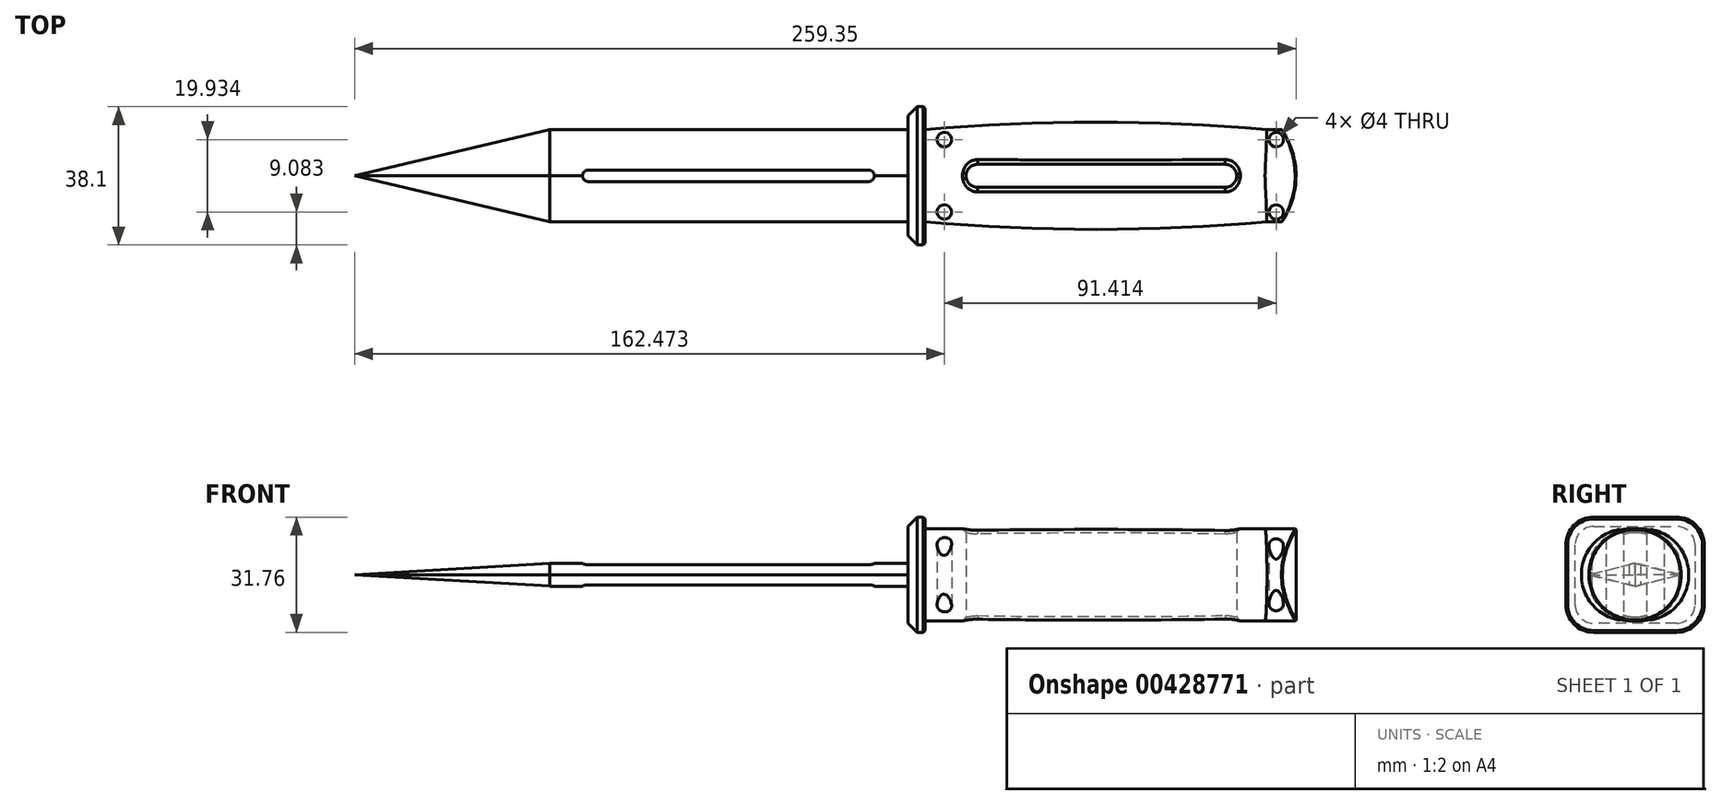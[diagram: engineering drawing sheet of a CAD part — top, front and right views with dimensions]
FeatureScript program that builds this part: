
annotation { "Feature Type Name" : "Feature", "Feature Type Description" : "" }
export const myFeature = defineFeature(function(context is Context, id is Id, definition is map)
    precondition{}
    {
        {
            var Q0;
            Q0=qCreatedBy(makeId("Top.planeOp"),FACE);
            var sketch = newSketch(context, id + "F0", { "sketchPlane" : qUnion([Q0])});
            skPoint(sketch, "E0.middle", {"position": v(0, 0) * mm});
            skLineSegment(sketch, "E1", {"start": v(-130.18, 0) * mm, "end": v(-76.43, 12.7) * mm});
            skLineSegment(sketch, "E2.MirrorCS", {"start": v(-130.18, 0) * mm, "end": v(-76.43, -12.7) * mm});
            skLineSegment(sketch, "E3", {"start": v(-76.43, 12.7) * mm, "end": v(22.22, 12.7) * mm});
            skLineSegment(sketch, "E4.MirrorCS", {"start": v(-76.43, -12.7) * mm, "end": v(22.22, -12.7) * mm});
            skLineSegment(sketch, "E5", {"start": v(-76.43, 12.7) * mm, "end": v(-76.43, 0) * mm});
            skLineSegment(sketch, "E6", {"start": v(-76.43, 0) * mm, "end": v(-76.43, -12.7) * mm});
            skLineSegment(sketch, "E7", {"start": v(-130.18, 0) * mm, "end": v(-76.43, 0) * mm});
            skLineSegment(sketch, "E8", {"start": v(22.22, 12.7) * mm, "end": v(22.22, -12.7) * mm});
            skLineSegment(sketch, "E9", {"start": v(22.22, 12.7) * mm, "end": v(22.22, 19.05) * mm});
            skLineSegment(sketch, "E10", {"start": v(22.22, 19.05) * mm, "end": v(27, 19.05) * mm});
            skLineSegment(sketch, "E11", {"start": v(27, 19.05) * mm, "end": v(27, 12.7) * mm});
            skLineSegment(sketch, "E12.MirrorCS", {"start": v(22.22, -12.7) * mm, "end": v(22.22, -19.05) * mm});
            skLineSegment(sketch, "E13.MirrorCS", {"start": v(22.22, -19.05) * mm, "end": v(27, -19.05) * mm});
            skLineSegment(sketch, "E14.MirrorCS", {"start": v(27, -19.05) * mm, "end": v(27, -12.7) * mm});
            skLineSegment(sketch, "E15", {"start": v(-65.78, 0) * mm, "end": v(11.43, 0) * mm});
            skArc(sketch, "E16.0.startCap", {"start": v(-65.78, -1.59) * mm, "mid": v(-67.36, 0) * mm, "end": v(-65.78, 1.59) * mm});
            skArc(sketch, "E16.0.endCap", {"start": v(11.43, 1.59) * mm, "mid": v(13.02, 0) * mm, "end": v(11.43, -1.59) * mm});
            skLineSegment(sketch, "E16.0.left", {"start": v(-65.78, 1.59) * mm, "end": v(11.43, 1.59) * mm});
            skLineSegment(sketch, "E16.0.right", {"start": v(-65.78, -1.59) * mm, "end": v(11.43, -1.59) * mm});
            skArc(sketch, "E17", {"start": v(121.17, 12.7) * mm, "mid": v(74.08, 14.77) * mm, "end": v(27, 12.7) * mm});
            skArc(sketch, "E18.MirrorCS", {"start": v(121.17, -12.7) * mm, "mid": v(74.08, -14.77) * mm, "end": v(27, -12.7) * mm});
            skArc(sketch, "E19", {"start": v(125.3, -12.7) * mm, "mid": v(129.17, 0) * mm, "end": v(125.3, 12.7) * mm});
            skFitSpline(sketch, "E20", {"points": [v(121.17, -12.7) * mm, v(125.3, -12.7) * mm], "startDerivative": vector(4.13, 0) * mm, "endDerivative": vector(4.13, 0) * mm});
            skFitSpline(sketch, "E21.MirrorCS", {"points": [v(121.17, 12.7) * mm, v(125.3, 12.7) * mm], "startDerivative": vector(4.13, 0) * mm, "endDerivative": vector(4.13, 0) * mm});
            skCircle(sketch, "E22", {"center": v(123.7, 9.97) * mm, "radius": 2 * mm});
            skCircle(sketch, "E23.MirrorC", {"center": v(123.7, -9.97) * mm, "radius": 2 * mm});
            skCircle(sketch, "E24", {"center": v(32.3, 9.97) * mm, "radius": 2 * mm});
            skCircle(sketch, "E25.MirrorC", {"center": v(32.3, -9.97) * mm, "radius": 2 * mm});
            skLineSegment(sketch, "E26", {"start": v(41.46, 0) * mm, "end": v(109.63, 0) * mm});
            skArc(sketch, "E27.0.startCap", {"start": v(41.46, -3.18) * mm, "mid": v(38.28, 0) * mm, "end": v(41.46, 3.18) * mm});
            skArc(sketch, "E27.0.endCap", {"start": v(109.63, 3.18) * mm, "mid": v(112.8, 0) * mm, "end": v(109.63, -3.18) * mm});
            skLineSegment(sketch, "E27.0.left", {"start": v(41.46, 3.18) * mm, "end": v(109.63, 3.18) * mm});
            skLineSegment(sketch, "E27.0.right", {"start": v(41.46, -3.18) * mm, "end": v(109.63, -3.18) * mm});
            skLineSegment(sketch, "E28", {"start": v(27, 12.7) * mm, "end": v(27, -12.7) * mm});
            skSolve(sketch);
        }
        {
            var Q0;
            Q0=makeQuery(id+"F0.imprint","IMPRINT",FACE,{"disambiguationData":[TD([[makeQuery(id+"F0.imprint","IMPRINT",EDGE,{"derivedFrom":sQuery(id+"F0.wireOp",EDGE,"E17")}),1.0]])]});
            extrude(context, id + "F1", {"entities" : qUnion([Q0]), "depth" : 25.4 * mm});
        }
        {
            var Q0;
            Q0=makeQuery(id+"F1.opExtrude","CAP_EDGE",EDGE,{"disambiguationData":[OSD([sQuery(id+"F0.wireOp",EDGE,"E17")])],"isStart":false});
            var Q1;
            Q1=makeQuery(id+"F1.opExtrude","CAP_EDGE",EDGE,{"disambiguationData":[OSD([sQuery(id+"F0.wireOp",EDGE,"E21.MirrorCS")])],"isStart":false});
            var Q2;
            Q2=makeQuery(id+"F1.opExtrude","CAP_EDGE",EDGE,{"disambiguationData":[OSD([sQuery(id+"F0.wireOp",EDGE,"E20")])],"isStart":false});
            var Q3;
            Q3=makeQuery(id+"F1.opExtrude","CAP_EDGE",EDGE,{"disambiguationData":[OSD([sQuery(id+"F0.wireOp",EDGE,"E18.MirrorCS")])],"isStart":false});
            var Q4;
            Q4=makeQuery(id+"F1.opExtrude","CAP_EDGE",EDGE,{"disambiguationData":[OSD([sQuery(id+"F0.wireOp",EDGE,"E18.MirrorCS")])],"isStart":true});
            var Q5;
            Q5=makeQuery(id+"F1.opExtrude","CAP_EDGE",EDGE,{"disambiguationData":[OSD([sQuery(id+"F0.wireOp",EDGE,"E20")])],"isStart":true});
            var Q6;
            Q6=makeQuery(id+"F1.opExtrude","CAP_EDGE",EDGE,{"disambiguationData":[OSD([sQuery(id+"F0.wireOp",EDGE,"E17")])],"isStart":true});
            var Q7;
            Q7=makeQuery(id+"F1.opExtrude","CAP_EDGE",EDGE,{"disambiguationData":[OSD([sQuery(id+"F0.wireOp",EDGE,"E21.MirrorCS")])],"isStart":true});
            fillet(context, id + "F2", {"entities" : qUnion([Q0, Q1, Q2, Q3, Q4, Q5, Q6, Q7]), "radius" : 12.67 * mm, "tangentPropagation" : true, "allowEdgeOverflow" : false});
        }
        {
            var Q0;
            Q0=makeQuery(id+"F0.imprint","IMPRINT",FACE,{"disambiguationData":[TD([[makeQuery(id+"F0.imprint","IMPRINT",EDGE,{"derivedFrom":sQuery(id+"F0.wireOp",EDGE,"E8")}),1.0]])]});
            extrude(context, id + "F3", {"entities" : qUnion([Q0]), "depth" : 28.57 * mm, "hasSecondDirection" : true, "secondDirectionOppositeDirection" : true, "secondDirectionDepth" : 3.17 * mm});
        }
        {
            var Q0;
            Q0=makeQuery(id+"F3.opExtrude","CAP_EDGE",EDGE,{"disambiguationData":[OSD([sQuery(id+"F0.wireOp",EDGE,"E10")])],"isStart":false});
            var Q1;
            Q1=makeQuery(id+"F3.opExtrude","CAP_EDGE",EDGE,{"disambiguationData":[OSD([sQuery(id+"F0.wireOp",EDGE,"E10")])],"isStart":true});
            var Q2;
            Q2=makeQuery(id+"F3.opExtrude","CAP_EDGE",EDGE,{"disambiguationData":[OSD([sQuery(id+"F0.wireOp",EDGE,"E13.MirrorCS")])],"isStart":true});
            var Q3;
            Q3=makeQuery(id+"F3.opExtrude","CAP_EDGE",EDGE,{"disambiguationData":[OSD([sQuery(id+"F0.wireOp",EDGE,"E13.MirrorCS")])],"isStart":false});
            fillet(context, id + "F4", {"entities" : qUnion([Q0, Q1, Q2, Q3]), "radius" : 7.62 * mm, "tangentPropagation" : true, "allowEdgeOverflow" : false});
        }
        {
            var Q0;
            Q0=makeQuery(id+"F3.opExtrude","CAP_EDGE",EDGE,{"disambiguationData":[OSD([sQuery(id+"F0.wireOp",EDGE,"E8"),sQuery(id+"F0.wireOp",EDGE,"E9"),sQuery(id+"F0.wireOp",EDGE,"E12.MirrorCS")])],"isStart":false});
            chamfer(context, id + "F5", {"entities" : qUnion([Q0]), "width" : 2.54 * mm, "tangentPropagation" : true});
        }
        {
            var Q0;
            Q0=makeQuery(id+"F3.opExtrude","CAP_EDGE",EDGE,{"disambiguationData":[OSD([sQuery(id+"F0.wireOp",EDGE,"E11"),sQuery(id+"F0.wireOp",EDGE,"E14.MirrorCS"),sQuery(id+"F0.wireOp",EDGE,"E28")])],"isStart":false});
            chamfer(context, id + "F6", {"entities" : qUnion([Q0]), "width" : 0.5 * mm, "tangentPropagation" : true});
        }
        {
            var Q0;
            Q0=makeQuery(id+"F2.opFillet","BLEND_EDGE",EDGE,{"blendedFrom":[makeQuery(id+"F1.opExtrude","CAP_EDGE",EDGE,{"disambiguationData":[OSD([sQuery(id+"F0.wireOp",EDGE,"E21.MirrorCS")])],"isStart":false}),makeQuery(id+"F1.opExtrude","SWEPT_FACE",FACE,{"disambiguationData":[OSD([sQuery(id+"F0.wireOp",EDGE,"E19")])]})],"blendedInto":[makeQuery(id+"F1.opExtrude","SWEPT_FACE",FACE,{"disambiguationData":[OSD([sQuery(id+"F0.wireOp",EDGE,"E19")])]})]});
            var Q1;
            Q1=makeQuery(id+"F2.opFillet","BLEND_EDGE",EDGE,{"blendedFrom":[makeQuery(id+"F1.opExtrude","CAP_EDGE",EDGE,{"disambiguationData":[OSD([sQuery(id+"F0.wireOp",EDGE,"E21.MirrorCS")])],"isStart":true}),makeQuery(id+"F1.opExtrude","SWEPT_FACE",FACE,{"disambiguationData":[OSD([sQuery(id+"F0.wireOp",EDGE,"E19")])]})],"blendedInto":[makeQuery(id+"F1.opExtrude","SWEPT_FACE",FACE,{"disambiguationData":[OSD([sQuery(id+"F0.wireOp",EDGE,"E19")])]})]});
            var Q2;
            Q2=makeQuery(id+"F2.opFillet","BLEND_EDGE",EDGE,{"blendedFrom":[makeQuery(id+"F1.opExtrude","CAP_EDGE",EDGE,{"disambiguationData":[OSD([sQuery(id+"F0.wireOp",EDGE,"E20")])],"isStart":true}),makeQuery(id+"F1.opExtrude","SWEPT_FACE",FACE,{"disambiguationData":[OSD([sQuery(id+"F0.wireOp",EDGE,"E19")])]})],"blendedInto":[makeQuery(id+"F1.opExtrude","SWEPT_FACE",FACE,{"disambiguationData":[OSD([sQuery(id+"F0.wireOp",EDGE,"E19")])]})]});
            var Q3;
            Q3=makeQuery(id+"F2.opFillet","BLEND_EDGE",EDGE,{"blendedFrom":[makeQuery(id+"F1.opExtrude","CAP_EDGE",EDGE,{"disambiguationData":[OSD([sQuery(id+"F0.wireOp",EDGE,"E20")])],"isStart":false}),makeQuery(id+"F1.opExtrude","SWEPT_FACE",FACE,{"disambiguationData":[OSD([sQuery(id+"F0.wireOp",EDGE,"E19")])]})],"blendedInto":[makeQuery(id+"F1.opExtrude","SWEPT_FACE",FACE,{"disambiguationData":[OSD([sQuery(id+"F0.wireOp",EDGE,"E19")])]})]});
            chamfer(context, id + "F7", {"entities" : qUnion([Q0, Q1, Q2, Q3]), "width" : 0.25 * mm, "tangentPropagation" : true});
        }
        {
            var Q0;
            Q0=makeQuery(id+"F2.opFillet","BLEND_EDGE",EDGE,{"blendedFrom":[makeQuery(id+"F1.opExtrude","CAP_EDGE",EDGE,{"disambiguationData":[OSD([sQuery(id+"F0.wireOp",EDGE,"E17")])],"isStart":false}),makeQuery(id+"F1.opExtrude","SWEPT_FACE",FACE,{"disambiguationData":[OSD([sQuery(id+"F0.wireOp",EDGE,"E27.0.left")])]})],"blendedInto":[makeQuery(id+"F1.opExtrude","SWEPT_FACE",FACE,{"disambiguationData":[OSD([sQuery(id+"F0.wireOp",EDGE,"E27.0.left")])]})]});
            var Q1;
            Q1=makeQuery(id+"F2.opFillet","BLEND_EDGE",EDGE,{"blendedFrom":[makeQuery(id+"F1.opExtrude","CAP_EDGE",EDGE,{"disambiguationData":[OSD([sQuery(id+"F0.wireOp",EDGE,"E17")])],"isStart":false}),makeQuery(id+"F1.opExtrude","SWEPT_FACE",FACE,{"disambiguationData":[OSD([sQuery(id+"F0.wireOp",EDGE,"E27.0.startCap")])]})],"blendedInto":[makeQuery(id+"F1.opExtrude","SWEPT_FACE",FACE,{"disambiguationData":[OSD([sQuery(id+"F0.wireOp",EDGE,"E27.0.startCap")])]})]});
            var Q2;
            Q2=makeQuery(id+"F1.opExtrude","CAP_EDGE",EDGE,{"disambiguationData":[OSD([sQuery(id+"F0.wireOp",EDGE,"E27.0.startCap")])],"isStart":false});
            var Q3;
            Q3=makeQuery(id+"F2.opFillet","BLEND_EDGE",EDGE,{"blendedFrom":[makeQuery(id+"F1.opExtrude","CAP_EDGE",EDGE,{"disambiguationData":[OSD([sQuery(id+"F0.wireOp",EDGE,"E18.MirrorCS")])],"isStart":false}),makeQuery(id+"F1.opExtrude","SWEPT_FACE",FACE,{"disambiguationData":[OSD([sQuery(id+"F0.wireOp",EDGE,"E27.0.startCap")])]})],"blendedInto":[makeQuery(id+"F1.opExtrude","SWEPT_FACE",FACE,{"disambiguationData":[OSD([sQuery(id+"F0.wireOp",EDGE,"E27.0.startCap")])]})]});
            var Q4;
            Q4=makeQuery(id+"F2.opFillet","BLEND_EDGE",EDGE,{"blendedFrom":[makeQuery(id+"F1.opExtrude","CAP_EDGE",EDGE,{"disambiguationData":[OSD([sQuery(id+"F0.wireOp",EDGE,"E18.MirrorCS")])],"isStart":false}),makeQuery(id+"F1.opExtrude","SWEPT_FACE",FACE,{"disambiguationData":[OSD([sQuery(id+"F0.wireOp",EDGE,"E27.0.right")])]})],"blendedInto":[makeQuery(id+"F1.opExtrude","SWEPT_FACE",FACE,{"disambiguationData":[OSD([sQuery(id+"F0.wireOp",EDGE,"E27.0.right")])]})]});
            var Q5;
            Q5=makeQuery(id+"F2.opFillet","BLEND_EDGE",EDGE,{"blendedFrom":[makeQuery(id+"F1.opExtrude","CAP_EDGE",EDGE,{"disambiguationData":[OSD([sQuery(id+"F0.wireOp",EDGE,"E18.MirrorCS")])],"isStart":false}),makeQuery(id+"F1.opExtrude","SWEPT_FACE",FACE,{"disambiguationData":[OSD([sQuery(id+"F0.wireOp",EDGE,"E27.0.endCap")])]})],"blendedInto":[makeQuery(id+"F1.opExtrude","SWEPT_FACE",FACE,{"disambiguationData":[OSD([sQuery(id+"F0.wireOp",EDGE,"E27.0.endCap")])]})]});
            var Q6;
            Q6=makeQuery(id+"F1.opExtrude","CAP_EDGE",EDGE,{"disambiguationData":[OSD([sQuery(id+"F0.wireOp",EDGE,"E27.0.endCap")])],"isStart":false});
            var Q7;
            Q7=makeQuery(id+"F2.opFillet","BLEND_EDGE",EDGE,{"blendedFrom":[makeQuery(id+"F1.opExtrude","CAP_EDGE",EDGE,{"disambiguationData":[OSD([sQuery(id+"F0.wireOp",EDGE,"E17")])],"isStart":false}),makeQuery(id+"F1.opExtrude","SWEPT_FACE",FACE,{"disambiguationData":[OSD([sQuery(id+"F0.wireOp",EDGE,"E27.0.endCap")])]})],"blendedInto":[makeQuery(id+"F1.opExtrude","SWEPT_FACE",FACE,{"disambiguationData":[OSD([sQuery(id+"F0.wireOp",EDGE,"E27.0.endCap")])]})]});
            var Q8;
            Q8=makeQuery(id+"F2.opFillet","BLEND_EDGE",EDGE,{"blendedFrom":[makeQuery(id+"F1.opExtrude","CAP_EDGE",EDGE,{"disambiguationData":[OSD([sQuery(id+"F0.wireOp",EDGE,"E17")])],"isStart":true}),makeQuery(id+"F1.opExtrude","SWEPT_FACE",FACE,{"disambiguationData":[OSD([sQuery(id+"F0.wireOp",EDGE,"E27.0.left")])]})],"blendedInto":[makeQuery(id+"F1.opExtrude","SWEPT_FACE",FACE,{"disambiguationData":[OSD([sQuery(id+"F0.wireOp",EDGE,"E27.0.left")])]})]});
            var Q9;
            Q9=makeQuery(id+"F2.opFillet","BLEND_EDGE",EDGE,{"blendedFrom":[makeQuery(id+"F1.opExtrude","CAP_EDGE",EDGE,{"disambiguationData":[OSD([sQuery(id+"F0.wireOp",EDGE,"E18.MirrorCS")])],"isStart":true}),makeQuery(id+"F1.opExtrude","SWEPT_FACE",FACE,{"disambiguationData":[OSD([sQuery(id+"F0.wireOp",EDGE,"E27.0.right")])]})],"blendedInto":[makeQuery(id+"F1.opExtrude","SWEPT_FACE",FACE,{"disambiguationData":[OSD([sQuery(id+"F0.wireOp",EDGE,"E27.0.right")])]})]});
            chamfer(context, id + "F8", {"entities" : qUnion([Q0, Q1, Q2, Q3, Q4, Q5, Q6, Q7, Q8, Q9]), "width" : 1.02 * mm, "tangentPropagation" : true});
        }
        {
            var Q0;
            Q0=makeQuery(id+"F0.imprint","IMPRINT",FACE,{"disambiguationData":[TD([[makeQuery(id+"F0.imprint","IMPRINT",EDGE,{"derivedFrom":sQuery(id+"F0.wireOp",EDGE,"E3")}),-1.0]])]});
            extrude(context, id + "F9", {"entities" : qUnion([Q0]), "depth" : 6.35 * mm});
        }
        {
            var Q0;
            Q0=makeQuery(id+"F9.opExtrude","SWEPT_BODY",BODY,{"disambiguationData":[OSD([sQuery(id+"F0.wireOp",EDGE,"E3"),sQuery(id+"F0.wireOp",EDGE,"E4.MirrorCS"),sQuery(id+"F0.wireOp",EDGE,"E5"),sQuery(id+"F0.wireOp",EDGE,"E6"),sQuery(id+"F0.wireOp",EDGE,"E8"),sQuery(id+"F0.wireOp",EDGE,"E16.0.startCap"),sQuery(id+"F0.wireOp",EDGE,"E16.0.endCap"),sQuery(id+"F0.wireOp",EDGE,"E16.0.left"),sQuery(id+"F0.wireOp",EDGE,"E16.0.right")])]});
            transform(context, id + "F10", {"entities" : qUnion([Q0]), "transformType" : TransformType.TRANSLATION_3D, "dx" : 0 * mm, "dy" : 0 * mm, "dz" : 9.52 * mm, "makeCopy" : false});
        }
        {
            var Q0;
            Q0=makeQuery(id+"F9.opExtrude","CAP_EDGE",EDGE,{"disambiguationData":[OSD([sQuery(id+"F0.wireOp",EDGE,"E4.MirrorCS")])],"isStart":false});
            var Q1;
            Q1=makeQuery(id+"F9.opExtrude","CAP_EDGE",EDGE,{"disambiguationData":[OSD([sQuery(id+"F0.wireOp",EDGE,"E3")])],"isStart":false});
            var Q2;
            Q2=makeQuery(id+"F9.opExtrude","CAP_EDGE",EDGE,{"disambiguationData":[OSD([sQuery(id+"F0.wireOp",EDGE,"E3")])],"isStart":true});
            var Q3;
            Q3=makeQuery(id+"F9.opExtrude","CAP_EDGE",EDGE,{"disambiguationData":[OSD([sQuery(id+"F0.wireOp",EDGE,"E4.MirrorCS")])],"isStart":true});
            chamfer(context, id + "F11", {"entities" : qUnion([Q0, Q1, Q2, Q3]), "chamferType" : ChamferType.TWO_OFFSETS, "width1" : 12.7 * mm, "oppositeDirection" : false, "width2" : 3.17 * mm, "tangentPropagation" : true});
        }
        {
            var Q0;
            Q0=makeQuery(id+"F0.imprint","IMPRINT",FACE,{"disambiguationData":[TD([[makeQuery(id+"F0.imprint","IMPRINT",EDGE,{"derivedFrom":sQuery(id+"F0.wireOp",EDGE,"E1")}),-1.0]])]});
            extrude(context, id + "F12", {"entities" : qUnion([Q0]), "depth" : 6.35 * mm});
        }
        {
            var Q0;
            Q0=makeQuery(id+"F12.opExtrude","SWEPT_BODY",BODY,{"disambiguationData":[OSD([sQuery(id+"F0.wireOp",EDGE,"E1"),sQuery(id+"F0.wireOp",EDGE,"E5"),sQuery(id+"F0.wireOp",EDGE,"E7")])]});
            transform(context, id + "F13", {"entities" : qUnion([Q0]), "transformType" : TransformType.TRANSLATION_3D, "dx" : 0 * mm, "dy" : 0 * mm, "dz" : 9.52 * mm, "makeCopy" : false});
        }
        {
            var Q0;
            Q0=makeQuery(id+"F0.imprint","IMPRINT",FACE,{"disambiguationData":[TD([[makeQuery(id+"F0.imprint","IMPRINT",EDGE,{"derivedFrom":sQuery(id+"F0.wireOp",EDGE,"E2.MirrorCS")}),1.0]])]});
            extrude(context, id + "F14", {"entities" : qUnion([Q0]), "depth" : 6.35 * mm});
        }
        {
            var Q0;
            Q0=makeQuery(id+"F14.opExtrude","SWEPT_BODY",BODY,{"disambiguationData":[OSD([sQuery(id+"F0.wireOp",EDGE,"E2.MirrorCS"),sQuery(id+"F0.wireOp",EDGE,"E6"),sQuery(id+"F0.wireOp",EDGE,"E7")])]});
            transform(context, id + "F15", {"entities" : qUnion([Q0]), "transformType" : TransformType.TRANSLATION_3D, "dx" : 0 * mm, "dy" : 0 * mm, "dz" : 9.52 * mm, "makeCopy" : false});
        }
        {
            var Q0;
            Q0=makeQuery(id+"F14.opExtrude","CAP_EDGE",EDGE,{"disambiguationData":[OSD([sQuery(id+"F0.wireOp",EDGE,"E2.MirrorCS")])],"isStart":false});
            var Q1;
            Q1=makeQuery(id+"F14.opExtrude","CAP_EDGE",EDGE,{"disambiguationData":[OSD([sQuery(id+"F0.wireOp",EDGE,"E2.MirrorCS")])],"isStart":true});
            chamfer(context, id + "F16", {"entities" : qUnion([Q0, Q1]), "chamferType" : ChamferType.TWO_OFFSETS, "width1" : 12.7 * mm, "oppositeDirection" : false, "width2" : 3.17 * mm, "tangentPropagation" : true});
        }
        {
            var Q0;
            Q0=makeQuery(id+"F12.opExtrude","CAP_EDGE",EDGE,{"disambiguationData":[OSD([sQuery(id+"F0.wireOp",EDGE,"E1")])],"isStart":true});
            var Q1;
            Q1=makeQuery(id+"F12.opExtrude","CAP_EDGE",EDGE,{"disambiguationData":[OSD([sQuery(id+"F0.wireOp",EDGE,"E1")])],"isStart":false});
            chamfer(context, id + "F17", {"entities" : qUnion([Q0, Q1]), "chamferType" : ChamferType.TWO_OFFSETS, "width1" : 12.7 * mm, "oppositeDirection" : false, "width2" : 3.17 * mm, "tangentPropagation" : true});
        }
    });
